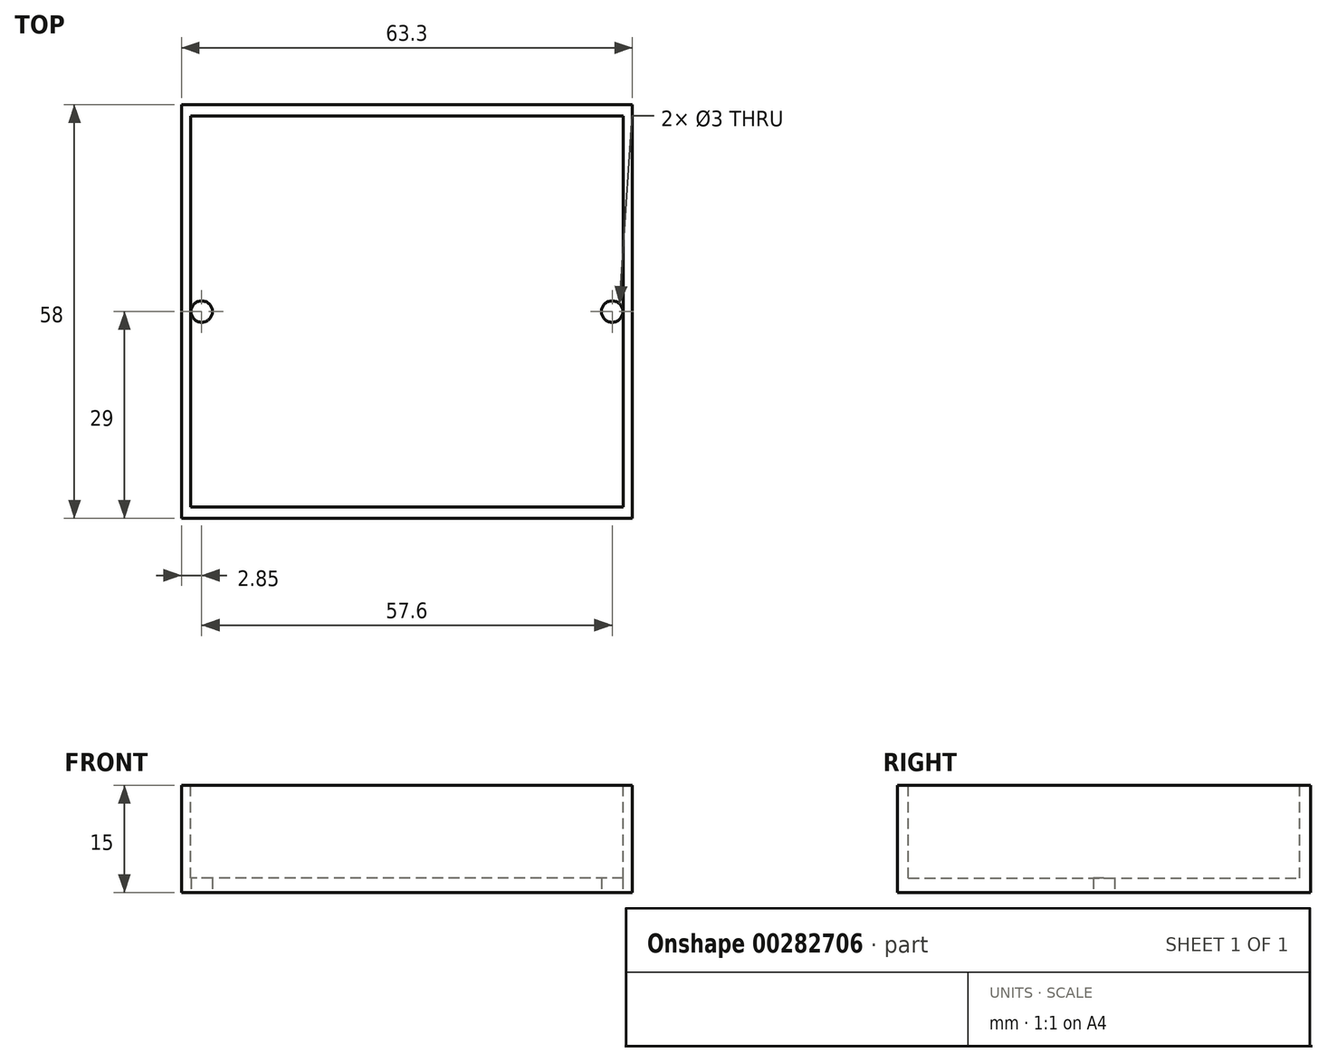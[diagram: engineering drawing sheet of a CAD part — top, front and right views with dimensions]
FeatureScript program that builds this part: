
annotation { "Feature Type Name" : "Feature", "Feature Type Description" : "" }
export const myFeature = defineFeature(function(context is Context, id is Id, definition is map)
    precondition{}
    {
        {
            var Q0;
            Q0=qCreatedBy(makeId("Top.planeOp"),FACE);
            var sketch = newSketch(context, id + "F0", { "sketchPlane" : qUnion([Q0])});
            skLineSegment(sketch, "E0.bottom", {"start": v(31.65, 29) * mm, "end": v(-31.65, 29) * mm});
            skLineSegment(sketch, "E0.top", {"start": v(31.65, -29) * mm, "end": v(-31.65, -29) * mm});
            skLineSegment(sketch, "E0.left", {"start": v(31.65, 29) * mm, "end": v(31.65, -29) * mm});
            skLineSegment(sketch, "E0.right", {"start": v(-31.65, 29) * mm, "end": v(-31.65, -29) * mm});
            skPoint(sketch, "E0.middle", {"position": v(0, 0) * mm});
            skSolve(sketch);
        }
        {
            var Q0;
            Q0=qSketchRegion(id+"F0",true);
            extrude(context, id + "F1", {"entities" : qUnion([Q0]), "depth" : 15 * mm});
        }
        {
            var Q0;
            Q0=makeQuery(id+"F1.opExtrude","CAP_FACE",FACE,{"disambiguationData":[OSD([sQuery(id+"F0.wireOp",EDGE,"E0.bottom"),sQuery(id+"F0.wireOp",EDGE,"E0.top"),sQuery(id+"F0.wireOp",EDGE,"E0.left"),sQuery(id+"F0.wireOp",EDGE,"E0.right")])],"isStart":false});
            var sketch = newSketch(context, id + "F2", { "sketchPlane" : qUnion([Q0])});
            skLineSegment(sketch, "E1.bottom", {"start": v(30.35, -27.45) * mm, "end": v(-30.35, -27.45) * mm});
            skLineSegment(sketch, "E1.top", {"start": v(30.35, 27.45) * mm, "end": v(-30.35, 27.45) * mm});
            skLineSegment(sketch, "E1.left", {"start": v(30.35, -27.45) * mm, "end": v(30.35, 27.45) * mm});
            skLineSegment(sketch, "E1.right", {"start": v(-30.35, -27.45) * mm, "end": v(-30.35, 27.45) * mm});
            skPoint(sketch, "E1.middle", {"position": v(0, 0) * mm});
            skSolve(sketch);
        }
        {
            var Q0;
            Q0=qSketchRegion(id+"F2",true);
            extrude(context, id + "F3", {"entities" : qUnion([Q0]), "operationType" : NewBodyOperationType.REMOVE, "oppositeDirection" : true, "depth" : 13 * mm});
        }
        {
            var Q0;
            Q0=makeQuery(id+"F1.opExtrude","CAP_FACE",FACE,{"disambiguationData":[OSD([sQuery(id+"F0.wireOp",EDGE,"E0.bottom"),sQuery(id+"F0.wireOp",EDGE,"E0.top"),sQuery(id+"F0.wireOp",EDGE,"E0.left"),sQuery(id+"F0.wireOp",EDGE,"E0.right")])],"isStart":true});
            var sketch = newSketch(context, id + "F4", { "sketchPlane" : qUnion([Q0])});
            skCircle(sketch, "E2", {"center": v(0, 0) * mm, "radius": 28.8 * mm, "construction": true});
            skCircle(sketch, "E3", {"center": v(28.8, 0) * mm, "radius": 1.5 * mm});
            skPoint(sketch, "E3.centerSnap0", {"position": v(31.65, 0) * mm});
            skCircle(sketch, "E4", {"center": v(-28.8, 0) * mm, "radius": 1.5 * mm});
            skSolve(sketch);
        }
        {
            var Q0;
            Q0=qSketchRegion(id+"F4",true);
            extrude(context, id + "F5", {"entities" : qUnion([Q0]), "operationType" : NewBodyOperationType.REMOVE, "endBound" : BoundingType.THROUGH_ALL, "oppositeDirection" : true, "depth" : 25 * mm});
        }
    });
